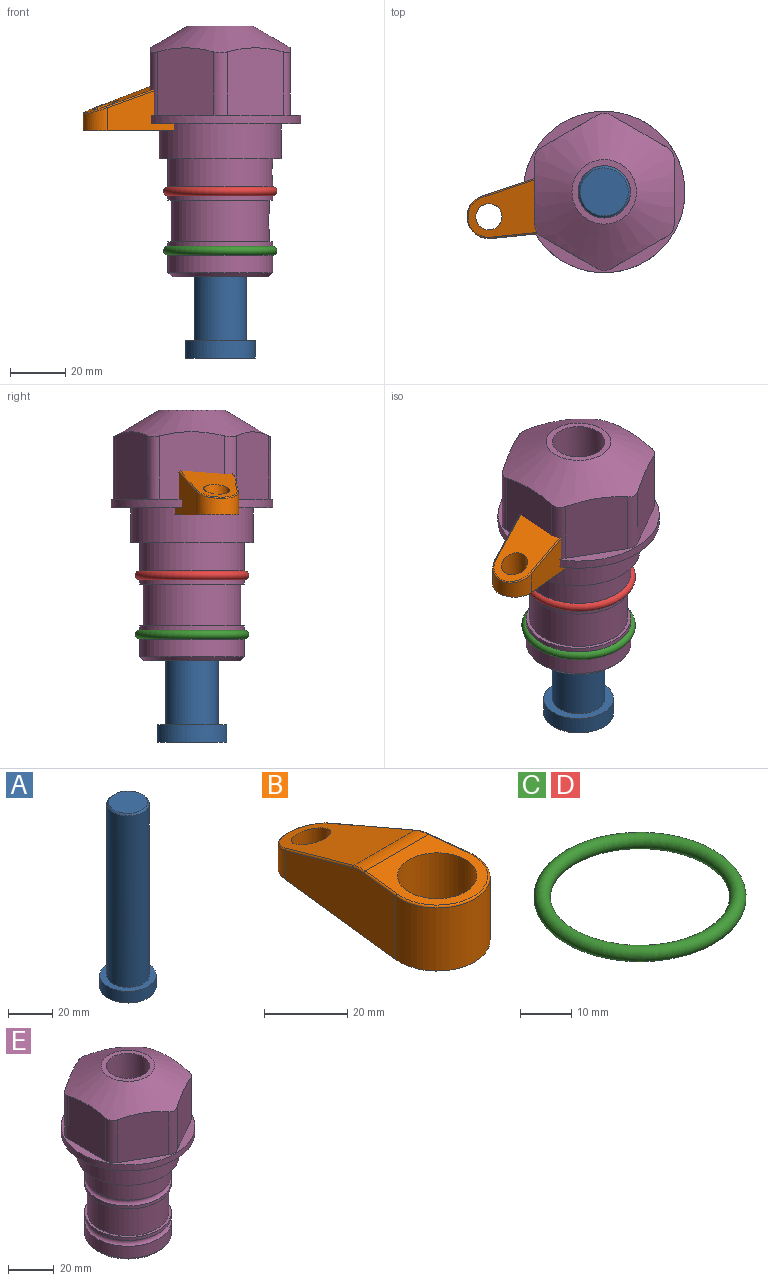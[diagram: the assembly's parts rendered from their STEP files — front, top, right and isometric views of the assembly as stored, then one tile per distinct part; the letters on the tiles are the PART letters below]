
ASSEMBLY  parts=5 mates=3
PART A: 6 faces, bbox 25.4x25.4x101.6 mm
  f0: plane 17.46x17.46mm, normal (0,0,1), area 239.5mm2, adj f5
  f1: plane 25.4x25.4mm, normal (0,0,-1), area 506.7mm2, adj f2
  f2: cylinder r=12.7mm len=25.4mm, axis (0,0,1), area 506.7mm2, adj f1,f3
  f3: plane 25.4x25.4mm, normal (0,0,1), area 221.7mm2, adj f2,f4
  f4: cylinder r=9.53mm len=94.46mm, axis (0,0,1), area 5653mm2, adj f3,f5
  f5: cone r=8.73mm half-angle=45deg, axis (0,0,-1), area 64.4mm2, adj f0,f4
PART B: 44 faces, bbox 27.5x64.5x19.1 mm
  f0: plane 2.3x0.95mm, normal (0,0,-1), area 1mm2, adj f25,f30,f34
  f1: plane 63.5x25.4mm, normal (0,0,-1), area 561.7mm2, adj f2,f3,f4,f5,f6,f7,f19,f20
  f2: cylinder r=12.7mm len=25.4mm, axis (0,0,-1), area 792.2mm2, adj f1,f3,f5,f13
  f3: plane 42.33x18.54mm, normal (0.99,0.11,0), area 647mm2, adj f1,f2,f4,f11,f12,f14
  f4: cylinder r=7.94mm len=15.78mm, axis (0,0,-1), area 158.6mm2, adj f1,f3,f5,f16
  f5: plane 42.33x18.54mm, normal (-0.99,0.11,0), area 647mm2, adj f1,f2,f4,f15,f17,f18
  f6: cylinder r=9.53mm len=19.05mm, axis (0,0,-1), area 1140.1mm2, adj f1,f8
  f7: cylinder r=4.76mm len=10.98mm, axis (0,0,-1), area 276.1mm2, adj f1,f9
  f8: plane 25.83x24.38mm, normal (0,0,1), area 262.2mm2, adj f6,f10,f11,f13,f15
  f9: plane 32.49x20.55mm, normal (0,0.34,0.94), area 489.9mm2, adj f7,f10,f14,f16,f18
  f10: cylinder r=12.7mm len=21.49mm, axis (-1,0,0), area 93.2mm2, adj f8,f9,f12,f17
  f11: cylinder r=0.51mm len=12.34mm, axis (0.11,-0.99,0), area 9.9mm2, adj f3,f8,f12,f13
  f12: bspline ~7.62x1.64mm, area 3.5mm2, adj f3,f10,f11,f14
  f13: torus R=12.19mm, axis (0,0,1), area 33.6mm2, adj f2,f8,f11,f15
  f14: cylinder r=0.51mm len=26.01mm, axis (0.1,-0.93,0.34), area 21.6mm2, adj f3,f9,f12,f16
  f15: cylinder r=0.51mm len=12.34mm, axis (0.11,0.99,0), area 9.9mm2, adj f5,f8,f13,f17
  f16: bspline ~15.78x7.05mm, area 15.7mm2, adj f4,f9,f14,f18
  f17: bspline ~7.62x1.64mm, area 3.5mm2, adj f5,f10,f15,f18
  f18: cylinder r=0.51mm len=26.01mm, axis (0.1,0.93,-0.34), area 21.6mm2, adj f5,f9,f16,f17
  f19: plane 21.6x14.29mm, normal (-0.99,-0.11,0), area 242.6mm2, adj f1,f26,f28,f34,f36,f38
  f20: plane 21.6x14.29mm, normal (0.99,-0.11,0), area 242.6mm2, adj f1,f27,f29,f37,f39,f41
  f21: cylinder r=12.7mm len=14.29mm, axis (0,0,-1), area 173.2mm2, adj f1,f26,f27,f30,f31,f33
  f22: cylinder r=7.94mm len=7.63mm, axis (0,0,-1), area 53.8mm2, adj f1,f28,f29,f42
  f23: plane 2.3x0.95mm, normal (0,0,-1), area 1mm2, adj f25,f33,f37
  f24: plane 17.94x12.32mm, normal (0,-0.34,-0.94), area 191.2mm2, adj f25,f38,f41,f42
  f25: cylinder r=9.53mm len=12.93mm, axis (-1,0,0), area 37.5mm2, adj f0,f23,f24,f31,f36,f39
  f26: cylinder r=1.59mm len=14.29mm, axis (0,0,-1), area 49mm2, adj f1,f19,f21,f32
  f27: cylinder r=1.59mm len=14.29mm, axis (0,0,-1), area 49mm2, adj f1,f20,f21,f35
  f28: cylinder r=1.59mm len=7.28mm, axis (0,0,-1), area 22.1mm2, adj f1,f19,f22,f40
  f29: cylinder r=1.59mm len=7.28mm, axis (0,0,-1), area 22.1mm2, adj f1,f20,f22,f43
  f30: torus R=14.29mm, axis (0,0,1), area 5.8mm2, adj f0,f21,f31,f32
  f31: bspline ~11.06x2.73mm, area 20.8mm2, adj f21,f25,f30,f33
  f32: sphere r=1.59mm, area 5.4mm2, adj f26,f30,f34
  f33: torus R=14.29mm, axis (0,0,1), area 5.8mm2, adj f21,f23,f31,f35
  f34: cylinder r=1.59mm len=1.68mm, axis (-0.11,0.99,0), area 2.4mm2, adj f0,f19,f32,f36
  f35: sphere r=1.59mm, area 5.4mm2, adj f27,f33,f37
  f36: bspline ~5.82x2.33mm, area 7.7mm2, adj f19,f25,f34,f38
  f37: cylinder r=1.59mm len=1.68mm, axis (0.11,0.99,0), area 2.4mm2, adj f20,f23,f35,f39
  f38: cylinder r=1.59mm len=18.33mm, axis (0.1,-0.93,0.34), area 46.7mm2, adj f19,f24,f36,f40
  f39: bspline ~5.82x2.33mm, area 7.7mm2, adj f20,f25,f37,f41
  f40: sphere r=1.59mm, area 3.6mm2, adj f28,f38,f42
  f41: cylinder r=1.59mm len=18.33mm, axis (0.1,0.93,-0.34), area 46.7mm2, adj f20,f24,f39,f43
  f42: bspline ~8.31x1.84mm, area 15.3mm2, adj f22,f24,f40,f43
  f43: sphere r=1.59mm, area 3.6mm2, adj f29,f41,f42
PART C: 1 faces, bbox 44.7x44.7x3.2 mm
  f0: torus R=19.05mm, axis (0,0,1), area 1193.9mm2
PART D: same geometry as C
PART E: 36 faces, bbox 58.7x58.7x91.2 mm
  f0: cylinder r=17.78mm len=35.56mm, axis (0,0,1), area 1670.8mm2, adj f23,f24,f31
  f1: cylinder r=19.05mm len=38.1mm, axis (0,0,1), area 1191.9mm2, adj f26,f27,f30
  f2: plane 58.66x58.66mm, normal (0,0,-1), area 1150.6mm2, adj f3,f28
  f3: cylinder r=29.33mm len=58.66mm, axis (0,0,-1), area 585.1mm2, adj f2,f4
  f4: plane 58.66x58.66mm, normal (0,0,1), area 475.9mm2, adj f3,f5,f6,f7,f8,f9,f10,f11
  f5: plane 24.5x20.32mm, normal (-0.5,0.87,0), area 562.8mm2, adj f4,f15,f16,f17
  f6: plane 24.5x20.32mm, normal (0.5,0.87,0), area 562.8mm2, adj f4,f14,f15,f17
  f7: plane 24.5x23.48mm, normal (1,0,0), area 562.8mm2, adj f4,f13,f14,f17
  f8: plane 24.5x20.32mm, normal (0.5,-0.87,0), area 562.8mm2, adj f4,f12,f13,f17
  f9: plane 24.5x20.32mm, normal (-0.5,-0.87,0), area 562.8mm2, adj f4,f11,f12,f17
  f10: plane 24.5x23.48mm, normal (-1,0,0), area 562.8mm2, adj f4,f11,f16,f17
  f11: cylinder r=5.08mm len=23.01mm, axis (0,0,-1), area 121.2mm2, adj f4,f9,f10,f17
  f12: cylinder r=5.08mm len=23.01mm, axis (0,0,-1), area 121.2mm2, adj f4,f8,f9,f17
  f13: cylinder r=5.08mm len=23.01mm, axis (0,0,-1), area 121.2mm2, adj f4,f7,f8,f17
  f14: cylinder r=5.08mm len=23.01mm, axis (0,0,-1), area 121.2mm2, adj f4,f6,f7,f17
  f15: cylinder r=5.08mm len=23.01mm, axis (0,0,-1), area 121.2mm2, adj f4,f5,f6,f17
  f16: cylinder r=5.08mm len=23.01mm, axis (0,0,-1), area 121.2mm2, adj f4,f5,f10,f17
  f17: cone r=11.73mm half-angle=60deg, axis (0,0,-1), area 2071.8mm2, adj f5,f6,f7,f8,f9,f10,f11,f12
  f18: plane 23.46x23.46mm, normal (0,0,1), area 147.4mm2, adj f17,f35
  f19: plane 34.93x34.93mm, normal (0,0,-1), area 958mm2, adj f29
  f20: cylinder r=19.05mm len=38.1mm, axis (0,0,1), area 760.1mm2, adj f21,f29
  f21: torus R=19.05mm, axis (0,0,1), area 565.3mm2, adj f20,f22
  f22: cylinder r=19.05mm len=38.1mm, axis (0,0,1), area 190mm2, adj f21,f23
  f23: plane 38.1x38.1mm, normal (0,0,1), area 146.9mm2, adj f0,f22
  f24: plane 38.1x38.1mm, normal (0,0,-1), area 146.9mm2, adj f0,f25
  f25: cylinder r=19.05mm len=38.1mm, axis (0,0,1), area 190mm2, adj f24,f26
  f26: torus R=19.05mm, axis (0,0,1), area 565.3mm2, adj f1,f25
  f27: plane 44.45x44.45mm, normal (0,0,-1), area 411.7mm2, adj f1,f28
  f28: cylinder r=22.23mm len=44.45mm, axis (0,0,1), area 1773.5mm2, adj f2,f27
  f29: cone r=19.05mm half-angle=45deg, axis (0,0,1), area 257.5mm2, adj f19,f20
  f30: cylinder r=3.17mm len=6.75mm, axis (-1,0,0), area 128mm2, adj f1,f33
  f31: cylinder r=3.17mm len=6.35mm, axis (-1,0,0), area 102.5mm2, adj f0,f33
  f32: plane 25.4x25.4mm, normal (0,0,1), area 506.7mm2, adj f33
  f33: cylinder r=12.7mm len=66.42mm, axis (0,0,-1), area 5236.2mm2, adj f30,f31,f32,f34
  f34: cone r=9.53mm half-angle=30deg, axis (0,0,-1), area 443.4mm2, adj f33,f35
  f35: cylinder r=9.53mm len=19.05mm, axis (0,0,-1), area 849mm2, adj f18,f34
PLACE A rot(axis=(0,0,-1),167.9deg) t=(0,0,-57.17)mm
PLACE B rot(axis=(0,0,1),102.1deg) t=(0,0,-2.56)mm
PLACE C t=(0,0,-21.59)mm
PLACE D at identity
PLACE E at identity fixed
MATE fastened C.f0 <-> E.f0  axis (0,0,1) through (0,0,-46.1)mm
MATE cylindrical A.f2 <-> E.f0  axis (0,0,1) through (0,0,-31.53)mm
MATE fastened B.f2 <-> A.f2  axis (0,0,1) through (0,0,16.49)mm
